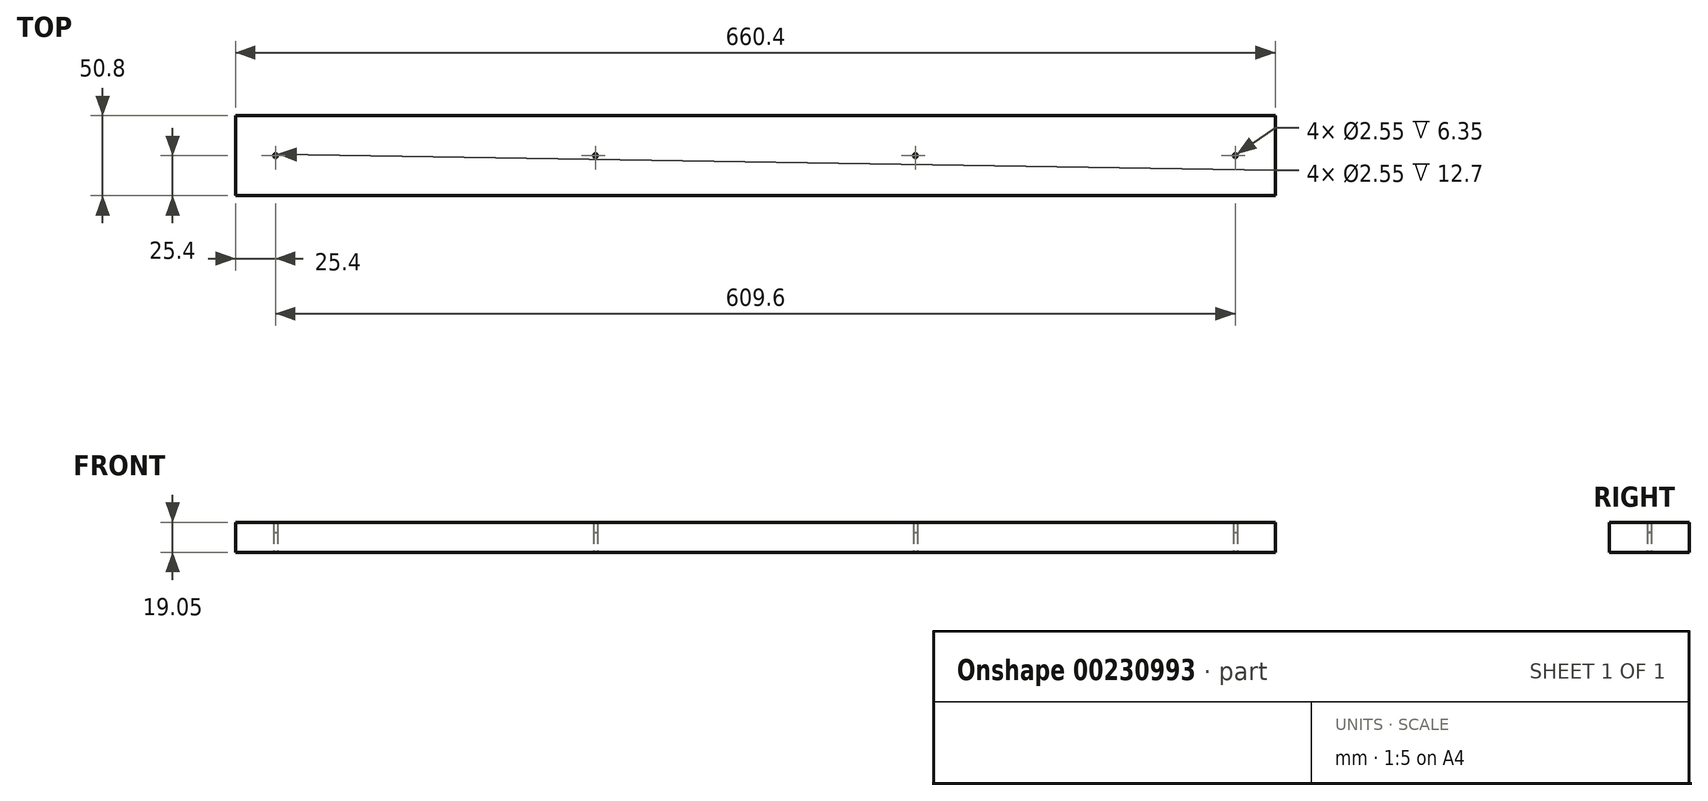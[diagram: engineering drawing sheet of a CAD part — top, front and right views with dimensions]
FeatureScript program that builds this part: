
annotation { "Feature Type Name" : "Feature", "Feature Type Description" : "" }
export const myFeature = defineFeature(function(context is Context, id is Id, definition is map)
    precondition{}
    {
        {
            var Q0;
            Q0=qCreatedBy(makeId("Top.planeOp"),FACE);
            var sketch = newSketch(context, id + "F0", { "sketchPlane" : qUnion([Q0])});
            skPoint(sketch, "E0", {"position": v(0, 0) * mm});
            skPoint(sketch, "E1.1.0.0", {"position": v(203.2, 0) * mm});
            skPoint(sketch, "E1.1.0.1", {"position": v(203.2, 0) * mm});
            skPoint(sketch, "E1.2.0.0", {"position": v(406.4, 0) * mm});
            skPoint(sketch, "E1.2.0.1", {"position": v(406.4, 0) * mm});
            skPoint(sketch, "E1.3.0.0", {"position": v(609.6, 0) * mm});
            skPoint(sketch, "E1.3.0.1", {"position": v(609.6, 0) * mm});
            skLineSegment(sketch, "E1.direction1", {"start": v(0, 0) * mm, "end": v(203.2, 0) * mm, "construction": true});
            skLineSegment(sketch, "E2.bottom", {"start": v(-25.4, -25.4) * mm, "end": v(635, -25.4) * mm});
            skLineSegment(sketch, "E2.top", {"start": v(-25.4, 25.4) * mm, "end": v(635, 25.4) * mm});
            skLineSegment(sketch, "E2.left", {"start": v(-25.4, -25.4) * mm, "end": v(-25.4, 25.4) * mm});
            skLineSegment(sketch, "E2.right", {"start": v(635, -25.4) * mm, "end": v(635, 25.4) * mm});
            skSolve(sketch);
        }
        {
            var Q0;
            Q0=makeQuery(id+"F0.imprint","IMPRINT",FACE,{"disambiguationData":[TD([[makeQuery(id+"F0.imprint","IMPRINT",EDGE,{"derivedFrom":sQuery(id+"F0.wireOp",EDGE,"E2.bottom")}),1.0]])]});
            extrude(context, id + "F1", {"entities" : qUnion([Q0]), "depth" : 19.05 * mm, "offsetDistance" : 25 * mm});
        }
        {
            var Q0;
            Q0=sQuery(id+"F0.wireOp",VERTEX,"E0");
            var Q1;
            Q1=sQuery(id+"F0.wireOp",VERTEX,"E1.1.0.1");
            var Q2;
            Q2=sQuery(id+"F0.wireOp",VERTEX,"E1.2.0.0");
            var Q3;
            Q3=sQuery(id+"F0.wireOp",VERTEX,"E1.3.0.0");
            var Q4;
            Q4=makeQuery(id+"F1.opExtrude","SWEPT_BODY",BODY,{"disambiguationData":[OSD([sQuery(id+"F0.wireOp",EDGE,"E2.bottom"),sQuery(id+"F0.wireOp",EDGE,"E2.top"),sQuery(id+"F0.wireOp",EDGE,"E2.left"),sQuery(id+"F0.wireOp",EDGE,"E2.right")])]});
            hole(context, id + "F2", {"style" : HoleStyle.C_BORE, "endStyle" : HoleEndStyle.THROUGH, "oppositeDirection" : true, "holeDiameter" : 1 / 101.6 * mm + 2.54 * mm, "cBoreDiameter" : 3 / 203.2 * mm + 2.54 * mm, "cBoreDepth" : 12.7 * mm, "isTappedThrough" : true, "tappedDepth" : 12 * mm, "tapClearance" : 3, "startFromSketch" : true, "locations" : qUnion([Q0, Q1, Q2, Q3]), "scope" : qUnion([Q4])});
        }
    });
